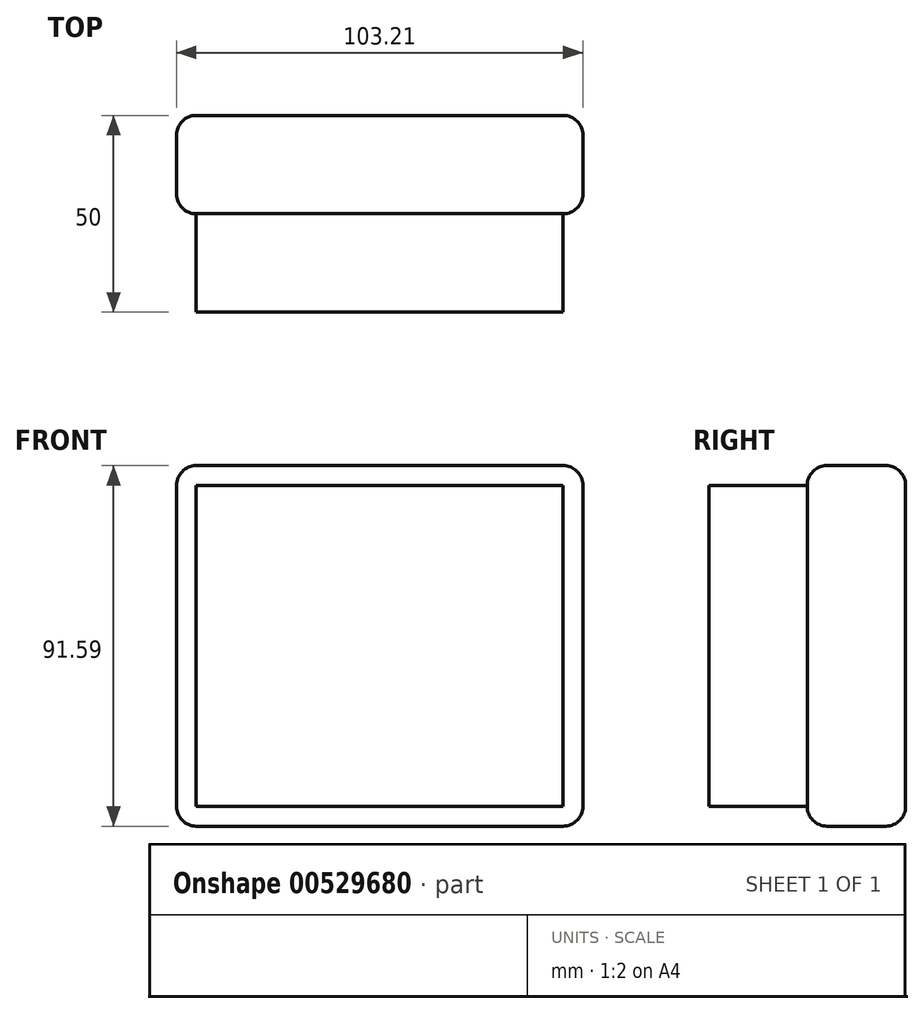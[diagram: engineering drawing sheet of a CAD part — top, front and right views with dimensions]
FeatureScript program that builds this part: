
annotation { "Feature Type Name" : "Feature", "Feature Type Description" : "" }
export const myFeature = defineFeature(function(context is Context, id is Id, definition is map)
    precondition{}
    {
        {
            var Q0;
            Q0=qCreatedBy(makeId("Front.planeOp"),FACE);
            var sketch = newSketch(context, id + "F0", { "sketchPlane" : qUnion([Q0])});
            skLineSegment(sketch, "E0.bottom", {"start": v(-66.53, 46.35) * mm, "end": v(36.68, 46.35) * mm});
            skLineSegment(sketch, "E0.top", {"start": v(-66.53, -45.24) * mm, "end": v(36.68, -45.24) * mm});
            skLineSegment(sketch, "E0.left", {"start": v(-66.53, 46.35) * mm, "end": v(-66.53, -45.24) * mm});
            skLineSegment(sketch, "E0.right", {"start": v(36.68, 46.35) * mm, "end": v(36.68, -45.24) * mm});
            skSolve(sketch);
        }
        {
            var Q0;
            Q0 = qSketchRegion(id + "F0", true);
            extrude(context, id + "F1", {"entities" : qUnion([Q0]), "depth" : 25 * mm, "offsetDistance" : 25 * mm});
        }
        {
            var Q0;
            Q0=makeQuery(id+"F1.opExtrude","CAP_FACE",FACE,{"disambiguationData":[OSD([sQuery(id+"F0.wireOp",EDGE,"E0.bottom"),sQuery(id+"F0.wireOp",EDGE,"E0.top"),sQuery(id+"F0.wireOp",EDGE,"E0.left"),sQuery(id+"F0.wireOp",EDGE,"E0.right")])],"isStart":false});
            var Q1;
            Q1=makeQuery(id+"F1.opExtrude","SWEPT_FACE",FACE,{"disambiguationData":[OSD([sQuery(id+"F0.wireOp",EDGE,"E0.bottom")])]});
            var Q2;
            Q2=makeQuery(id+"F1.opExtrude","SWEPT_FACE",FACE,{"disambiguationData":[OSD([sQuery(id+"F0.wireOp",EDGE,"E0.right")])]});
            var Q3;
            Q3=makeQuery(id+"F1.opExtrude","SWEPT_FACE",FACE,{"disambiguationData":[OSD([sQuery(id+"F0.wireOp",EDGE,"E0.top")])]});
            var Q4;
            Q4=makeQuery(id+"F1.opExtrude","SWEPT_FACE",FACE,{"disambiguationData":[OSD([sQuery(id+"F0.wireOp",EDGE,"E0.left")])]});
            fillet(context, id + "F2", {"entities" : qUnion([Q0, Q1, Q2, Q3, Q4]), "radius" : 5 * mm, "tangentPropagation" : true, "allowEdgeOverflow" : false});
        }
        {
            var Q0;
            Q0=makeQuery(id+"F1.opExtrude","CAP_FACE",FACE,{"disambiguationData":[OSD([sQuery(id+"F0.wireOp",EDGE,"E0.bottom"),sQuery(id+"F0.wireOp",EDGE,"E0.top"),sQuery(id+"F0.wireOp",EDGE,"E0.left"),sQuery(id+"F0.wireOp",EDGE,"E0.right")])],"isStart":false});
            extrude(context, id + "F3", {"entities" : qUnion([Q0]), "operationType" : NewBodyOperationType.ADD, "depth" : 25 * mm, "offsetDistance" : 25 * mm});
        }
    });
